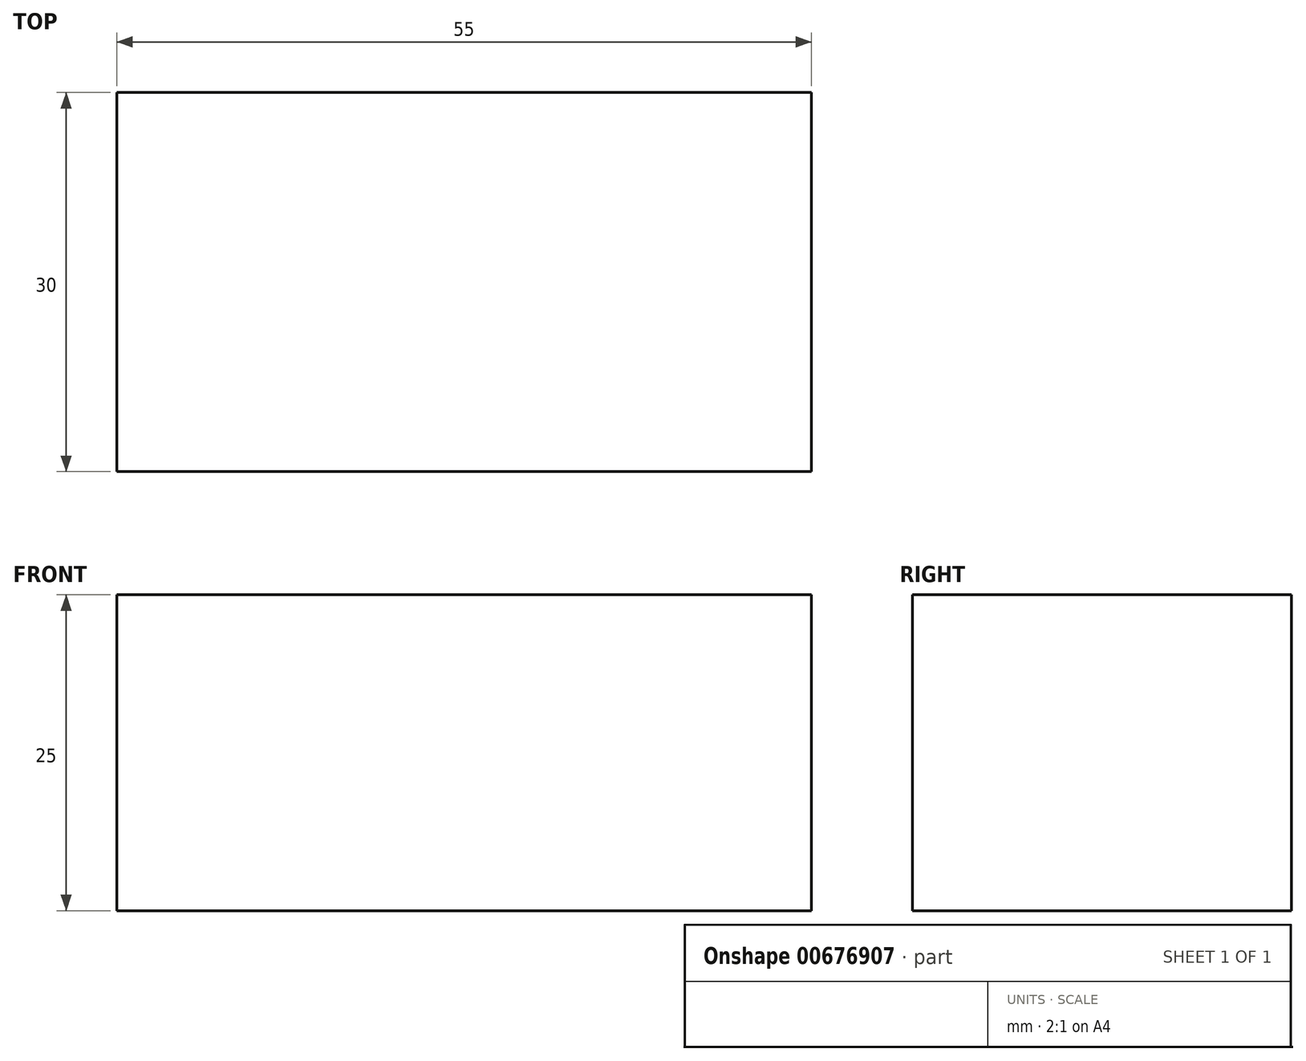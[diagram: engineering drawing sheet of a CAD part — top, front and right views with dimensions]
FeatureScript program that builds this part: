
annotation { "Feature Type Name" : "Feature", "Feature Type Description" : "" }
export const myFeature = defineFeature(function(context is Context, id is Id, definition is map)
    precondition{}
    {
        {
            var Q0;
            Q0=qCreatedBy(makeId("Top.planeOp"),FACE);
            var sketch = newSketch(context, id + "F0", { "sketchPlane" : qUnion([Q0])});
            skLineSegment(sketch, "E0.bottom", {"start": v(-27.5, 15) * mm, "end": v(27.5, 15) * mm});
            skLineSegment(sketch, "E0.top", {"start": v(-27.5, -15) * mm, "end": v(27.5, -15) * mm});
            skLineSegment(sketch, "E0.left", {"start": v(-27.5, 15) * mm, "end": v(-27.5, -15) * mm});
            skLineSegment(sketch, "E0.right", {"start": v(27.5, 15) * mm, "end": v(27.5, -15) * mm});
            skPoint(sketch, "E0.middle", {"position": v(0, 0) * mm});
            skSolve(sketch);
        }
        {
            var Q0;
            Q0 = qSketchRegion(id + "F0", true);
            extrude(context, id + "F1", {"entities" : qUnion([Q0]), "depth" : 25 * mm, "offsetDistance" : 25 * mm});
        }
        {
            var Q0;
            Q0=makeQuery(id+"F1.opExtrude","SWEPT_FACE",FACE,{"disambiguationData":[OSD([sQuery(id+"F0.wireOp",EDGE,"E0.top")])]});
            var sketch = newSketch(context, id + "F2", { "sketchPlane" : qUnion([Q0])});
            skSolve(sketch);
        }
    });
